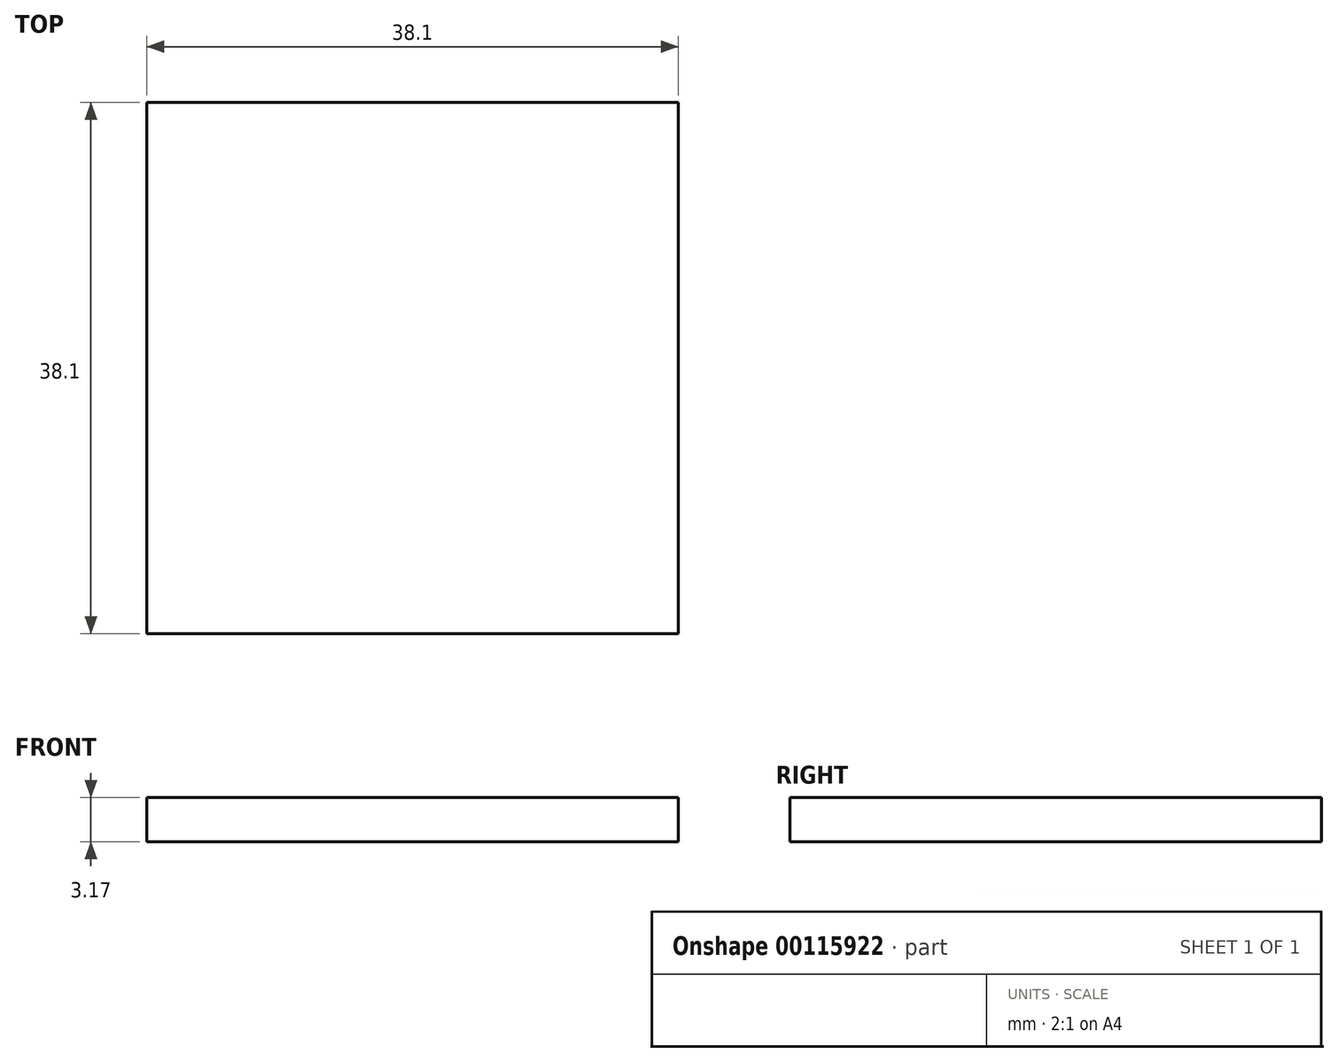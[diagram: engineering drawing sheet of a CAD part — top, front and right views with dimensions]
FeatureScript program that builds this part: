
annotation { "Feature Type Name" : "Feature", "Feature Type Description" : "" }
export const myFeature = defineFeature(function(context is Context, id is Id, definition is map)
    precondition{}
    {
        {
            var Q0;
            Q0=qCreatedBy(makeId("Top.planeOp"),FACE);
            var sketch = newSketch(context, id + "F0", { "sketchPlane" : qUnion([Q0])});
            skLineSegment(sketch, "E0.bottom", {"start": v(-28.59, 14.27) * mm, "end": v(9.51, 14.27) * mm});
            skLineSegment(sketch, "E0.top", {"start": v(-28.59, -23.83) * mm, "end": v(9.51, -23.83) * mm});
            skLineSegment(sketch, "E0.left", {"start": v(-28.59, 14.27) * mm, "end": v(-28.59, -23.83) * mm});
            skLineSegment(sketch, "E0.right", {"start": v(9.51, 14.27) * mm, "end": v(9.51, -23.83) * mm});
            skSolve(sketch);
        }
        {
            var Q0;
            Q0=makeQuery(id+"F0.imprint","IMPRINT",FACE,{"disambiguationData":[TD([[makeQuery(id+"F0.imprint","IMPRINT",EDGE,{"derivedFrom":sQuery(id+"F0.wireOp",EDGE,"E0.bottom")}),-1.0]])]});
            extrude(context, id + "F1", {"entities" : qUnion([Q0]), "depth" : 3.17 * mm});
        }
    });
